# Revit family: PRD_FrankeWS_GrpVlvs_SIRIUSDevice-connectingValve_ZSIRW001
name_source: partatom
category: Plumbing Fixtures
revit_build: Autodesk Revit 2018 (Build: 20190510_1515(x64)
units: mm (PartAtom-declared; Revit-internal decimal feet)

## family parameters
Cut with Voids When Loaded = Yes
Host = Face
OmniClass Number = 23.45.05.14.17
OmniClass Title = Showers
Part Type = Normal
Room Calculation Point = No
Round Connector Dimension = Use Diameter
Shared = Yes

## types (1)
- ZSIRW001
    AssetType = Fixed
    BIMObjectName = PRD_AR_GripValves_SIRIUSDevice-connectingValve_ZSIRW001
    Category = Pr_40_20_87_35, Grip valves
    CloseOffRating = 0.0 Pa
    Default Elevation = 2000 mm  [stored 6.56168 ft]
    Description = Appliance connection fitting DN 15, for wall mounting, with triangular knob, non-return valve, pipe interrupter, screw coupling for hoses and head part G 3/4 x G 1/2 B.
    DiameterNominal = 15  [stored 0.0492126 ft]
    DurationUnit = year
    Features = screw coupling for hoses and head part G 3/4 x G 1/2 B
    FlowCoefficient = 0
    GrossWeight = 0.46 kg
    IfcExportAs = IfcValveType
    IfcExportType = USERDEFINED
    Manufacturer = KWC Group AG
    ManufacturerName = KWC Group AG
    ManufacturerURL = www.kwc.com
    Model = ZSIRW001
    ModelNumber = 2000101470
    ModelReference = ZSIRW001
    Name = SIRIUS Device-connecting valve ZSIRW001
    NetWeight = 0.41 kg
    NominalDepth = 0 mm  [stored 0 ft]
    NominalHeight = 0 mm  [stored 0 ft]
    NominalWidth = 0 mm  [stored 0 ft]
    ProductInformation = https://pim.kwc.com
    Quantity = 1
    QuantityUom = Piece
    Status = New
    TestPressure = 0.0 Pa
    URL = www.kwc.com
    Uniclass2015Code = Pr_40_20_87_35
    Uniclass2015Title = Grip valves
    Uniclass2015Version = Products v1.23
    ValveMaterial = PRD_AR_ChromatedBrass_HighPolished
    ValveMechanism = OTHER
    ValveOperation = HYDRAULIC
    ValvePattern = STRAIGHT_2_PORT
    Version = 1
    WarrantyDurationUnit = year
    WorkingPressure = 0.0 Pa

note: [stored X ft] marks values corroborated as IEEE doubles in the binary element streams (Revit-internal decimal feet)

## geometry (parser evidence)
native form markers: Sweep x2
no freeform markers — native parametric forms only
